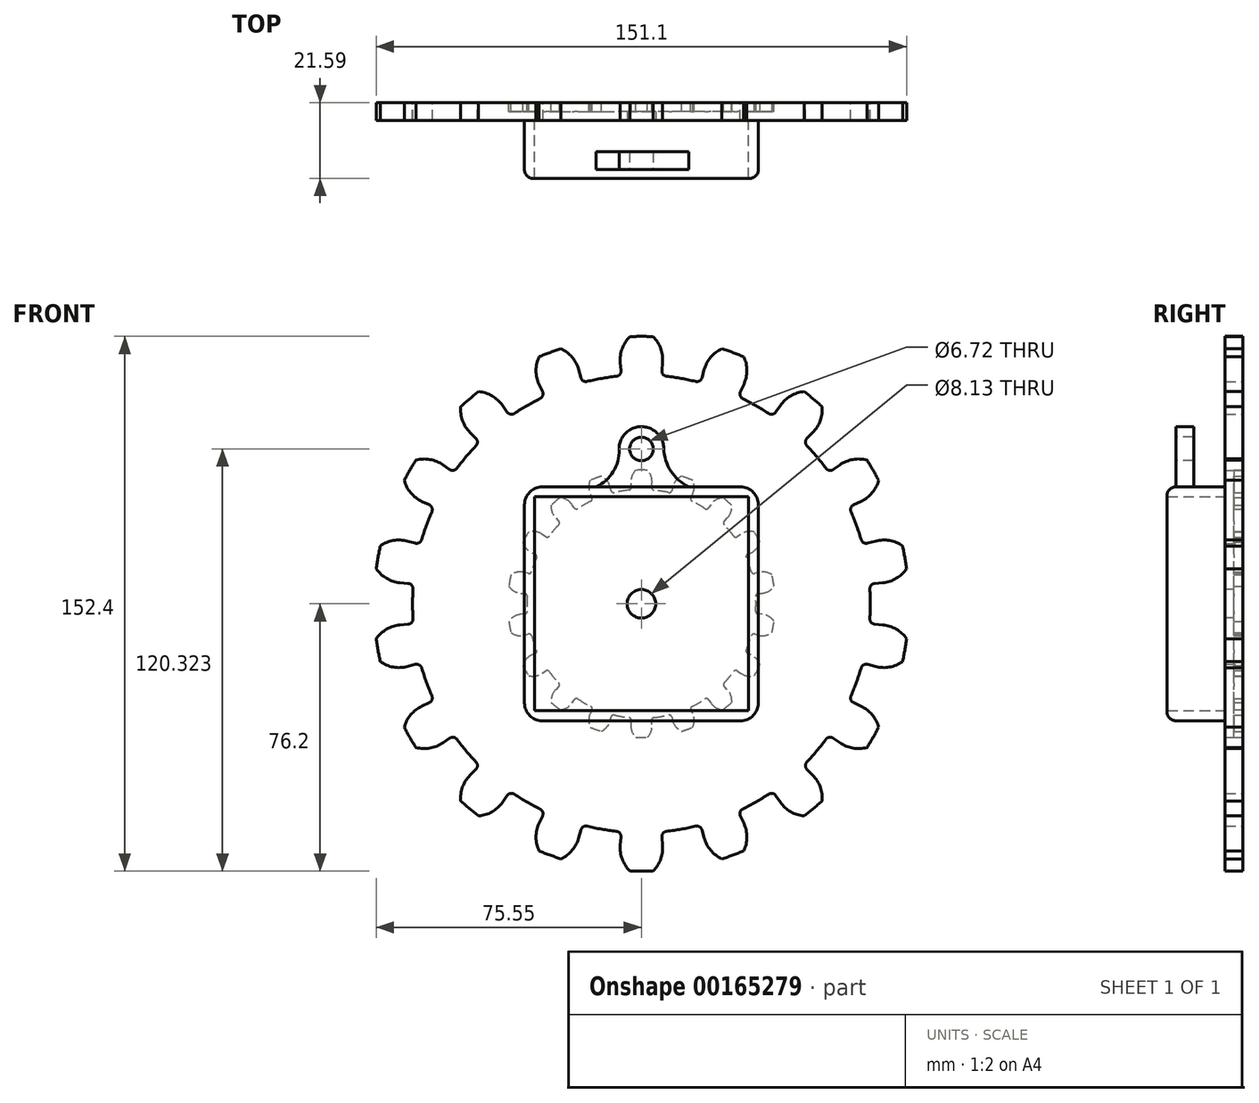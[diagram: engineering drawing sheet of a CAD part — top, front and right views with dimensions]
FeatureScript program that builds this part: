
annotation { "Feature Type Name" : "Feature", "Feature Type Description" : "" }
export const myFeature = defineFeature(function(context is Context, id is Id, definition is map)
    precondition{}
    {
        {
            var Q0;
            Q0=qCreatedBy(makeId("Front.planeOp"),FACE);
            var sketch = newSketch(context, id + "F0", { "sketchPlane" : qUnion([Q0])});
            skArc(sketch, "E0", {"start": v(0, 76.2) * mm, "mid": v(-1.66, 76.18) * mm, "end": v(-3.32, 76.13) * mm});
            skLineSegment(sketch, "E1", {"start": v(0, 0) * mm, "end": v(0, 76.2) * mm, "construction": true});
            skLineSegment(sketch, "E2", {"start": v(0, 0) * mm, "end": v(-11.32, 64.22) * mm});
            skLineSegment(sketch, "E3", {"start": v(0, 0) * mm, "end": v(-6.64, 75.91) * mm, "construction": true});
            skLineSegment(sketch, "E4", {"start": v(0, 0) * mm, "end": v(-3.32, 76.13) * mm, "construction": true});
            skArc(sketch, "E5", {"start": v(-3.32, 76.13) * mm, "mid": v(-5.49, 72.75) * mm, "end": v(-6.02, 68.77) * mm});
            skLineSegment(sketch, "E6", {"start": v(-6.02, 68.77) * mm, "end": v(-5.68, 64.97) * mm, "construction": true});
            skLineSegment(sketch, "E7", {"start": v(-6.02, 68.77) * mm, "end": v(-5.68, 64.97) * mm});
            skLineSegment(sketch, "E8", {"start": v(0, 76.2) * mm, "end": v(0, 0) * mm});
            skArc(sketch, "E9.trimOffspring", {"start": v(-5.68, 64.97) * mm, "mid": v(-8.51, 64.66) * mm, "end": v(-11.32, 64.22) * mm});
            skLineSegment(sketch, "E10.MirrorCS", {"start": v(0, 0) * mm, "end": v(11.32, 64.22) * mm});
            skArc(sketch, "E11.MirrorCS", {"start": v(5.68, 64.97) * mm, "mid": v(8.51, 64.66) * mm, "end": v(11.32, 64.22) * mm});
            skLineSegment(sketch, "E12.MirrorCS", {"start": v(6.02, 68.77) * mm, "end": v(5.68, 64.97) * mm, "construction": true});
            skArc(sketch, "E13.MirrorCS", {"start": v(3.32, 76.13) * mm, "mid": v(5.49, 72.75) * mm, "end": v(6.02, 68.77) * mm});
            skArc(sketch, "E14.MirrorCS", {"start": v(0, 76.2) * mm, "mid": v(1.66, 76.18) * mm, "end": v(3.32, 76.13) * mm});
            skLineSegment(sketch, "E15", {"start": v(5.68, 64.97) * mm, "end": v(6.02, 68.77) * mm});
            skSolve(sketch);
        }
        {
            var Q0;
            Q0 = qSketchRegion(id + "F0", true);
            extrude(context, id + "F1", {"entities" : qUnion([Q0]), "depth" : 12.7 * mm});
        }
        {
            var Q0;
            Q0=makeQuery(id+"F1.opExtrude","SWEPT_EDGE",EDGE,{"disambiguationData":[OSD([sQuery(id+"F0.wireOp",EDGE,"E11.MirrorCS"),sQuery(id+"F0.wireOp",EDGE,"E15")])]});
            var Q1;
            Q1=makeQuery(id+"F1.opExtrude","SWEPT_EDGE",EDGE,{"disambiguationData":[OSD([sQuery(id+"F0.wireOp",EDGE,"E7"),sQuery(id+"F0.wireOp",EDGE,"E9.trimOffspring")])]});
            fillet(context, id + "F2", {"entities" : qUnion([Q0, Q1]), "radius" : 1.52 * mm, "tangentPropagation" : true, "allowEdgeOverflow" : false});
        }
        {
            var Q0;
            Q0=makeQuery(id+"F1.opExtrude","SWEPT_BODY",BODY,{"disambiguationData":[OSD([sQuery(id+"F0.wireOp",EDGE,"E0"),sQuery(id+"F0.wireOp",EDGE,"E2"),sQuery(id+"F0.wireOp",EDGE,"E5"),sQuery(id+"F0.wireOp",EDGE,"E7"),sQuery(id+"F0.wireOp",EDGE,"E9.trimOffspring"),sQuery(id+"F0.wireOp",EDGE,"E10.MirrorCS"),sQuery(id+"F0.wireOp",EDGE,"E11.MirrorCS"),sQuery(id+"F0.wireOp",EDGE,"E13.MirrorCS"),sQuery(id+"F0.wireOp",EDGE,"E14.MirrorCS"),sQuery(id+"F0.wireOp",EDGE,"E15")])]});
            var Q1;
            Q1=makeQuery(id+"F1.opExtrude","SWEPT_EDGE",EDGE,{"disambiguationData":[OSD([sQuery(id+"F0.wireOp",EDGE,"E2"),sQuery(id+"F0.wireOp",EDGE,"E8"),sQuery(id+"F0.wireOp",EDGE,"E10.MirrorCS")])]});
            circularPattern(context, id + "F3", {"operationType" : NewBodyOperationType.ADD, "entities" : qUnion([Q0]), "axis" : qUnion([Q1]), "angle" : 20 * degree, "instanceCount" : 18});
        }
        {
            var Q0;
            {var subQ0=makeQuery(id+"F1.opExtrude","CAP_FACE",FACE,{"disambiguationData":[OSD([sQuery(id+"F0.wireOp",EDGE,"E0"),sQuery(id+"F0.wireOp",EDGE,"E2"),sQuery(id+"F0.wireOp",EDGE,"E5"),sQuery(id+"F0.wireOp",EDGE,"E7"),sQuery(id+"F0.wireOp",EDGE,"E9.trimOffspring"),sQuery(id+"F0.wireOp",EDGE,"E10.MirrorCS"),sQuery(id+"F0.wireOp",EDGE,"E11.MirrorCS"),sQuery(id+"F0.wireOp",EDGE,"E13.MirrorCS"),sQuery(id+"F0.wireOp",EDGE,"E14.MirrorCS"),sQuery(id+"F0.wireOp",EDGE,"E15")])],"isStart":false});Q0=makeQuery(id+"F3.boolean.opBoolean","MERGE",FACE,{"derivedFrom":[subQ0,makeQuery(id+"F3.opPattern","COPY",FACE,{"derivedFrom":subQ0,"instanceName":"1"}),makeQuery(id+"F3.opPattern","COPY",FACE,{"derivedFrom":subQ0,"instanceName":"2"}),makeQuery(id+"F3.opPattern","COPY",FACE,{"derivedFrom":subQ0,"instanceName":"3"}),makeQuery(id+"F3.opPattern","COPY",FACE,{"derivedFrom":subQ0,"instanceName":"4"}),makeQuery(id+"F3.opPattern","COPY",FACE,{"derivedFrom":subQ0,"instanceName":"5"}),makeQuery(id+"F3.opPattern","COPY",FACE,{"derivedFrom":subQ0,"instanceName":"6"}),makeQuery(id+"F3.opPattern","COPY",FACE,{"derivedFrom":subQ0,"instanceName":"7"}),makeQuery(id+"F3.opPattern","COPY",FACE,{"derivedFrom":subQ0,"instanceName":"8"}),makeQuery(id+"F3.opPattern","COPY",FACE,{"derivedFrom":subQ0,"instanceName":"9"}),makeQuery(id+"F3.opPattern","COPY",FACE,{"derivedFrom":subQ0,"instanceName":"10"}),makeQuery(id+"F3.opPattern","COPY",FACE,{"derivedFrom":subQ0,"instanceName":"11"}),makeQuery(id+"F3.opPattern","COPY",FACE,{"derivedFrom":subQ0,"instanceName":"12"}),makeQuery(id+"F3.opPattern","COPY",FACE,{"derivedFrom":subQ0,"instanceName":"13"}),makeQuery(id+"F3.opPattern","COPY",FACE,{"derivedFrom":subQ0,"instanceName":"14"}),makeQuery(id+"F3.opPattern","COPY",FACE,{"derivedFrom":subQ0,"instanceName":"15"}),makeQuery(id+"F3.opPattern","COPY",FACE,{"derivedFrom":subQ0,"instanceName":"16"}),makeQuery(id+"F3.opPattern","COPY",FACE,{"derivedFrom":subQ0,"instanceName":"17"})]});}
            var sketch = newSketch(context, id + "F4", { "sketchPlane" : qUnion([Q0])});
            skLineSegment(sketch, "E16.bottom", {"start": v(-30.48, 30.48) * mm, "end": v(30.48, 30.48) * mm});
            skLineSegment(sketch, "E16.top", {"start": v(-30.48, -30.48) * mm, "end": v(30.48, -30.48) * mm});
            skLineSegment(sketch, "E16.left", {"start": v(-30.48, 30.48) * mm, "end": v(-30.48, -30.48) * mm});
            skLineSegment(sketch, "E16.right", {"start": v(30.48, 30.48) * mm, "end": v(30.48, -30.48) * mm});
            skLineSegment(sketch, "E17", {"start": v(-33.32, 33.32) * mm, "end": v(-33.32, -33.32) * mm});
            skLineSegment(sketch, "E18", {"start": v(-33.32, -33.32) * mm, "end": v(33.32, -33.32) * mm});
            skLineSegment(sketch, "E19", {"start": v(33.32, -33.32) * mm, "end": v(33.32, 33.32) * mm});
            skLineSegment(sketch, "E20", {"start": v(33.32, 33.32) * mm, "end": v(-33.32, 33.32) * mm});
            skLineSegment(sketch, "E21", {"start": v(-30.48, 30.48) * mm, "end": v(30.48, -30.48) * mm, "construction": true});
            skLineSegment(sketch, "E22", {"start": v(-30.48, -30.48) * mm, "end": v(30.48, 30.48) * mm, "construction": true});
            skSolve(sketch);
        }
        {
            var Q0;
            Q0 = qSketchRegion(id + "F4", true);
            extrude(context, id + "F5", {"entities" : qUnion([Q0]), "depth" : 16.5 * mm});
        }
        {
            var Q0;
            {var subQ0=sQuery(id+"F0.wireOp",EDGE,"E15");var subQ1=sQuery(id+"F0.wireOp",EDGE,"E11.MirrorCS");var subQ3=sQuery(id+"F0.wireOp",EDGE,"E13.MirrorCS");var subQ5=sQuery(id+"F0.wireOp",EDGE,"E14.MirrorCS");var subQ6=sQuery(id+"F0.wireOp",EDGE,"E0");var subQ12=sQuery(id+"F0.wireOp",EDGE,"E7");var subQ15=sQuery(id+"F0.wireOp",EDGE,"E9.trimOffspring");var subQ19=sQuery(id+"F0.wireOp",EDGE,"E5");var subQ20=makeQuery(id+"F1.opExtrude","SWEPT_FACE",FACE,{"disambiguationData":[OSD([subQ19])]});var subQ21=makeQuery(id+"F1.opExtrude","CAP_FACE",FACE,{"disambiguationData":[OSD([subQ6,sQuery(id+"F0.wireOp",EDGE,"E2"),subQ19,subQ12,subQ15,sQuery(id+"F0.wireOp",EDGE,"E10.MirrorCS"),subQ1,subQ3,subQ5,subQ0])],"isStart":false});Q0=makeQuery(id+"F5.boolean.opBoolean","SPLIT",FACE,{"disambiguationData":[TD([subQ20])],"derivedFrom":makeQuery(id+"F3.boolean.opBoolean","MERGE",FACE,{"derivedFrom":[subQ21,makeQuery(id+"F3.opPattern","COPY",FACE,{"derivedFrom":subQ21,"instanceName":"1"}),makeQuery(id+"F3.opPattern","COPY",FACE,{"derivedFrom":subQ21,"instanceName":"2"}),makeQuery(id+"F3.opPattern","COPY",FACE,{"derivedFrom":subQ21,"instanceName":"3"}),makeQuery(id+"F3.opPattern","COPY",FACE,{"derivedFrom":subQ21,"instanceName":"4"}),makeQuery(id+"F3.opPattern","COPY",FACE,{"derivedFrom":subQ21,"instanceName":"5"}),makeQuery(id+"F3.opPattern","COPY",FACE,{"derivedFrom":subQ21,"instanceName":"6"}),makeQuery(id+"F3.opPattern","COPY",FACE,{"derivedFrom":subQ21,"instanceName":"7"}),makeQuery(id+"F3.opPattern","COPY",FACE,{"derivedFrom":subQ21,"instanceName":"8"}),makeQuery(id+"F3.opPattern","COPY",FACE,{"derivedFrom":subQ21,"instanceName":"9"}),makeQuery(id+"F3.opPattern","COPY",FACE,{"derivedFrom":subQ21,"instanceName":"10"}),makeQuery(id+"F3.opPattern","COPY",FACE,{"derivedFrom":subQ21,"instanceName":"11"}),makeQuery(id+"F3.opPattern","COPY",FACE,{"derivedFrom":subQ21,"instanceName":"12"}),makeQuery(id+"F3.opPattern","COPY",FACE,{"derivedFrom":subQ21,"instanceName":"13"}),makeQuery(id+"F3.opPattern","COPY",FACE,{"derivedFrom":subQ21,"instanceName":"14"}),makeQuery(id+"F3.opPattern","COPY",FACE,{"derivedFrom":subQ21,"instanceName":"15"}),makeQuery(id+"F3.opPattern","COPY",FACE,{"derivedFrom":subQ21,"instanceName":"16"}),makeQuery(id+"F3.opPattern","COPY",FACE,{"derivedFrom":subQ21,"instanceName":"17"})]})});}
            var sketch = newSketch(context, id + "F6", { "sketchPlane" : qUnion([Q0])});
            skCircle(sketch, "E23", {"center": v(0, 0) * mm, "radius": 4.06 * mm});
            skSolve(sketch);
        }
        {
            var Q0;
            Q0 = qSketchRegion(id + "F6", true);
            extrude(context, id + "F7", {"entities" : qUnion([Q0]), "operationType" : NewBodyOperationType.REMOVE, "oppositeDirection" : true, "depth" : 25.4 * mm});
        }
        {
            var Q0;
            Q0=makeQuery(id+"F5.opExtrude","SWEPT_EDGE",EDGE,{"disambiguationData":[OSD([sQuery(id+"F4.wireOp",EDGE,"E19"),sQuery(id+"F4.wireOp",EDGE,"E20")])]});
            var Q1;
            Q1=makeQuery(id+"F5.opExtrude","SWEPT_EDGE",EDGE,{"disambiguationData":[OSD([sQuery(id+"F4.wireOp",EDGE,"E17"),sQuery(id+"F4.wireOp",EDGE,"E20")])]});
            var Q2;
            Q2=makeQuery(id+"F5.opExtrude","SWEPT_EDGE",EDGE,{"disambiguationData":[OSD([sQuery(id+"F4.wireOp",EDGE,"E17"),sQuery(id+"F4.wireOp",EDGE,"E18")])]});
            var Q3;
            Q3=makeQuery(id+"F5.opExtrude","SWEPT_EDGE",EDGE,{"disambiguationData":[OSD([sQuery(id+"F4.wireOp",EDGE,"E18"),sQuery(id+"F4.wireOp",EDGE,"E19")])]});
            fillet(context, id + "F8", {"entities" : qUnion([Q0, Q1, Q2, Q3]), "radius" : 5.08 * mm, "tangentPropagation" : true, "allowEdgeOverflow" : false});
        }
        {
            var Q0;
            Q0=makeQuery(id+"F5.opExtrude","CAP_EDGE",EDGE,{"disambiguationData":[OSD([sQuery(id+"F4.wireOp",EDGE,"E18")])],"isStart":false});
            var Q1;
            Q1=makeQuery(id+"F5.opExtrude","CAP_EDGE",EDGE,{"disambiguationData":[OSD([sQuery(id+"F4.wireOp",EDGE,"E19")])],"isStart":false});
            var Q2;
            Q2=makeQuery(id+"F5.opExtrude","CAP_EDGE",EDGE,{"disambiguationData":[OSD([sQuery(id+"F4.wireOp",EDGE,"E20")])],"isStart":false});
            var Q3;
            Q3=makeQuery(id+"F5.opExtrude","CAP_EDGE",EDGE,{"disambiguationData":[OSD([sQuery(id+"F4.wireOp",EDGE,"E17")])],"isStart":false});
            var Q4;
            {var subQ0=sQuery(id+"F4.wireOp",EDGE,"E18");var subQ1=sQuery(id+"F4.wireOp",EDGE,"E17");Q4=makeQuery(id+"F8.opFillet","BLEND_EDGE",EDGE,{"blendedFrom":[makeQuery(id+"F5.opExtrude","SWEPT_EDGE",EDGE,{"disambiguationData":[OSD([subQ1,subQ0])]}),makeQuery(id+"F5.opExtrude","CAP_FACE",FACE,{"disambiguationData":[OSD([sQuery(id+"F4.wireOp",EDGE,"E16.bottom"),sQuery(id+"F4.wireOp",EDGE,"E16.top"),sQuery(id+"F4.wireOp",EDGE,"E16.left"),sQuery(id+"F4.wireOp",EDGE,"E16.right"),subQ1,subQ0,sQuery(id+"F4.wireOp",EDGE,"E19"),sQuery(id+"F4.wireOp",EDGE,"E20")])],"isStart":false})],"blendedInto":[makeQuery(id+"F5.opExtrude","CAP_FACE",FACE,{"disambiguationData":[OSD([sQuery(id+"F4.wireOp",EDGE,"E16.bottom"),sQuery(id+"F4.wireOp",EDGE,"E16.top"),sQuery(id+"F4.wireOp",EDGE,"E16.left"),sQuery(id+"F4.wireOp",EDGE,"E16.right"),subQ1,subQ0,sQuery(id+"F4.wireOp",EDGE,"E19"),sQuery(id+"F4.wireOp",EDGE,"E20")])],"isStart":false})]});}
            var Q5;
            {var subQ0=sQuery(id+"F4.wireOp",EDGE,"E19");var subQ1=sQuery(id+"F4.wireOp",EDGE,"E18");Q5=makeQuery(id+"F8.opFillet","BLEND_EDGE",EDGE,{"blendedFrom":[makeQuery(id+"F5.opExtrude","SWEPT_EDGE",EDGE,{"disambiguationData":[OSD([subQ1,subQ0])]}),makeQuery(id+"F5.opExtrude","CAP_FACE",FACE,{"disambiguationData":[OSD([sQuery(id+"F4.wireOp",EDGE,"E16.bottom"),sQuery(id+"F4.wireOp",EDGE,"E16.top"),sQuery(id+"F4.wireOp",EDGE,"E16.left"),sQuery(id+"F4.wireOp",EDGE,"E16.right"),sQuery(id+"F4.wireOp",EDGE,"E17"),subQ1,subQ0,sQuery(id+"F4.wireOp",EDGE,"E20")])],"isStart":false})],"blendedInto":[makeQuery(id+"F5.opExtrude","CAP_FACE",FACE,{"disambiguationData":[OSD([sQuery(id+"F4.wireOp",EDGE,"E16.bottom"),sQuery(id+"F4.wireOp",EDGE,"E16.top"),sQuery(id+"F4.wireOp",EDGE,"E16.left"),sQuery(id+"F4.wireOp",EDGE,"E16.right"),sQuery(id+"F4.wireOp",EDGE,"E17"),subQ1,subQ0,sQuery(id+"F4.wireOp",EDGE,"E20")])],"isStart":false})]});}
            var Q6;
            {var subQ0=sQuery(id+"F4.wireOp",EDGE,"E20");var subQ1=sQuery(id+"F4.wireOp",EDGE,"E19");Q6=makeQuery(id+"F8.opFillet","BLEND_EDGE",EDGE,{"blendedFrom":[makeQuery(id+"F5.opExtrude","SWEPT_EDGE",EDGE,{"disambiguationData":[OSD([subQ1,subQ0])]}),makeQuery(id+"F5.opExtrude","CAP_FACE",FACE,{"disambiguationData":[OSD([sQuery(id+"F4.wireOp",EDGE,"E16.bottom"),sQuery(id+"F4.wireOp",EDGE,"E16.top"),sQuery(id+"F4.wireOp",EDGE,"E16.left"),sQuery(id+"F4.wireOp",EDGE,"E16.right"),sQuery(id+"F4.wireOp",EDGE,"E17"),sQuery(id+"F4.wireOp",EDGE,"E18"),subQ1,subQ0])],"isStart":false})],"blendedInto":[makeQuery(id+"F5.opExtrude","CAP_FACE",FACE,{"disambiguationData":[OSD([sQuery(id+"F4.wireOp",EDGE,"E16.bottom"),sQuery(id+"F4.wireOp",EDGE,"E16.top"),sQuery(id+"F4.wireOp",EDGE,"E16.left"),sQuery(id+"F4.wireOp",EDGE,"E16.right"),sQuery(id+"F4.wireOp",EDGE,"E17"),sQuery(id+"F4.wireOp",EDGE,"E18"),subQ1,subQ0])],"isStart":false})]});}
            var Q7;
            {var subQ0=sQuery(id+"F4.wireOp",EDGE,"E20");var subQ1=sQuery(id+"F4.wireOp",EDGE,"E17");Q7=makeQuery(id+"F8.opFillet","BLEND_EDGE",EDGE,{"blendedFrom":[makeQuery(id+"F5.opExtrude","SWEPT_EDGE",EDGE,{"disambiguationData":[OSD([subQ1,subQ0])]}),makeQuery(id+"F5.opExtrude","CAP_FACE",FACE,{"disambiguationData":[OSD([sQuery(id+"F4.wireOp",EDGE,"E16.bottom"),sQuery(id+"F4.wireOp",EDGE,"E16.top"),sQuery(id+"F4.wireOp",EDGE,"E16.left"),sQuery(id+"F4.wireOp",EDGE,"E16.right"),subQ1,sQuery(id+"F4.wireOp",EDGE,"E18"),sQuery(id+"F4.wireOp",EDGE,"E19"),subQ0])],"isStart":false})],"blendedInto":[makeQuery(id+"F5.opExtrude","CAP_FACE",FACE,{"disambiguationData":[OSD([sQuery(id+"F4.wireOp",EDGE,"E16.bottom"),sQuery(id+"F4.wireOp",EDGE,"E16.top"),sQuery(id+"F4.wireOp",EDGE,"E16.left"),sQuery(id+"F4.wireOp",EDGE,"E16.right"),subQ1,sQuery(id+"F4.wireOp",EDGE,"E18"),sQuery(id+"F4.wireOp",EDGE,"E19"),subQ0])],"isStart":false})]});}
            fillet(context, id + "F9", {"entities" : qUnion([Q0, Q1, Q2, Q3, Q4, Q5, Q6, Q7]), "radius" : 2.54 * mm, "tangentPropagation" : true, "allowEdgeOverflow" : false});
        }
        {
            var Q0;
            Q0=makeQuery(id+"F5.opExtrude","CAP_FACE",FACE,{"disambiguationData":[OSD([sQuery(id+"F4.wireOp",EDGE,"E16.bottom"),sQuery(id+"F4.wireOp",EDGE,"E16.top"),sQuery(id+"F4.wireOp",EDGE,"E16.left"),sQuery(id+"F4.wireOp",EDGE,"E16.right"),sQuery(id+"F4.wireOp",EDGE,"E17"),sQuery(id+"F4.wireOp",EDGE,"E18"),sQuery(id+"F4.wireOp",EDGE,"E19"),sQuery(id+"F4.wireOp",EDGE,"E20")])],"isStart":false});
            var sketch = newSketch(context, id + "F10", { "sketchPlane" : qUnion([Q0])});
            skArc(sketch, "E24", {"start": v(6.36, 44.3) * mm, "mid": v(-0.18, 50.48) * mm, "end": v(-6.36, 43.93) * mm});
            skCircle(sketch, "E25", {"center": v(0, 44.12) * mm, "radius": 3.36 * mm});
            skArc(sketch, "E26", {"start": v(-12.9, 33.32) * mm, "mid": v(-8.04, 37.65) * mm, "end": v(-6.36, 43.93) * mm});
            skArc(sketch, "E27", {"start": v(6.36, 44.3) * mm, "mid": v(8.39, 37.8) * mm, "end": v(13.51, 33.32) * mm});
            skLineSegment(sketch, "E28", {"start": v(-6.04, 33.32) * mm, "end": v(-12.9, 33.32) * mm});
            skLineSegment(sketch, "E29", {"start": v(6.66, 33.32) * mm, "end": v(13.51, 33.32) * mm});
            skLineSegment(sketch, "E30", {"start": v(-12.9, 33.32) * mm, "end": v(13.51, 33.32) * mm});
            skSolve(sketch);
        }
        {
            var Q0;
            Q0 = qSketchRegion(id + "F10", true);
            extrude(context, id + "F11", {"entities" : qUnion([Q0]), "oppositeDirection" : true, "depth" : 5.08 * mm});
        }
        {
            var Q0;
            Q0=makeQuery(id+"F1.opExtrude","SWEPT_BODY",BODY,{"disambiguationData":[OSD([sQuery(id+"F0.wireOp",EDGE,"E0"),sQuery(id+"F0.wireOp",EDGE,"E2"),sQuery(id+"F0.wireOp",EDGE,"E5"),sQuery(id+"F0.wireOp",EDGE,"E7"),sQuery(id+"F0.wireOp",EDGE,"E9.trimOffspring"),sQuery(id+"F0.wireOp",EDGE,"E10.MirrorCS"),sQuery(id+"F0.wireOp",EDGE,"E11.MirrorCS"),sQuery(id+"F0.wireOp",EDGE,"E13.MirrorCS"),sQuery(id+"F0.wireOp",EDGE,"E14.MirrorCS"),sQuery(id+"F0.wireOp",EDGE,"E15")])]});
            var Q1;
            Q1=qCreatedBy(makeId("Origin.pointOp"),VERTEX);
            transform(context, id + "F12", {"entities" : qUnion([Q0]), "transformType" : TransformType.SCALE_UNIFORMLY, "scale" : .5, "scalePoint" : qUnion([Q1]), "makeCopy" : true});
        }
        {
            var Q0;
            {var subQ0=makeQuery(id+"F1.opExtrude","CAP_FACE",FACE,{"disambiguationData":[OSD([sQuery(id+"F0.wireOp",EDGE,"E0"),sQuery(id+"F0.wireOp",EDGE,"E2"),sQuery(id+"F0.wireOp",EDGE,"E5"),sQuery(id+"F0.wireOp",EDGE,"E7"),sQuery(id+"F0.wireOp",EDGE,"E9.trimOffspring"),sQuery(id+"F0.wireOp",EDGE,"E10.MirrorCS"),sQuery(id+"F0.wireOp",EDGE,"E11.MirrorCS"),sQuery(id+"F0.wireOp",EDGE,"E13.MirrorCS"),sQuery(id+"F0.wireOp",EDGE,"E14.MirrorCS"),sQuery(id+"F0.wireOp",EDGE,"E15")])],"isStart":true});Q0=makeQuery(id+"F12.opPattern","COPY",FACE,{"derivedFrom":makeQuery(id+"F3.boolean.opBoolean","MERGE",FACE,{"derivedFrom":[subQ0,makeQuery(id+"F3.opPattern","COPY",FACE,{"derivedFrom":subQ0,"instanceName":"1"}),makeQuery(id+"F3.opPattern","COPY",FACE,{"derivedFrom":subQ0,"instanceName":"2"}),makeQuery(id+"F3.opPattern","COPY",FACE,{"derivedFrom":subQ0,"instanceName":"3"}),makeQuery(id+"F3.opPattern","COPY",FACE,{"derivedFrom":subQ0,"instanceName":"4"}),makeQuery(id+"F3.opPattern","COPY",FACE,{"derivedFrom":subQ0,"instanceName":"5"}),makeQuery(id+"F3.opPattern","COPY",FACE,{"derivedFrom":subQ0,"instanceName":"6"}),makeQuery(id+"F3.opPattern","COPY",FACE,{"derivedFrom":subQ0,"instanceName":"7"}),makeQuery(id+"F3.opPattern","COPY",FACE,{"derivedFrom":subQ0,"instanceName":"8"}),makeQuery(id+"F3.opPattern","COPY",FACE,{"derivedFrom":subQ0,"instanceName":"9"}),makeQuery(id+"F3.opPattern","COPY",FACE,{"derivedFrom":subQ0,"instanceName":"10"}),makeQuery(id+"F3.opPattern","COPY",FACE,{"derivedFrom":subQ0,"instanceName":"11"}),makeQuery(id+"F3.opPattern","COPY",FACE,{"derivedFrom":subQ0,"instanceName":"12"}),makeQuery(id+"F3.opPattern","COPY",FACE,{"derivedFrom":subQ0,"instanceName":"13"}),makeQuery(id+"F3.opPattern","COPY",FACE,{"derivedFrom":subQ0,"instanceName":"14"}),makeQuery(id+"F3.opPattern","COPY",FACE,{"derivedFrom":subQ0,"instanceName":"15"}),makeQuery(id+"F3.opPattern","COPY",FACE,{"derivedFrom":subQ0,"instanceName":"16"}),makeQuery(id+"F3.opPattern","COPY",FACE,{"derivedFrom":subQ0,"instanceName":"17"})]}),"instanceName":"1"});}
            extrude(context, id + "F13", {"entities" : qUnion([Q0]), "operationType" : NewBodyOperationType.REMOVE, "oppositeDirection" : true, "depth" : 2.54 * mm});
        }
        {
            var Q0;
            Q0=makeQuery(id+"F1.opExtrude","SWEPT_BODY",BODY,{"disambiguationData":[OSD([sQuery(id+"F0.wireOp",EDGE,"E0"),sQuery(id+"F0.wireOp",EDGE,"E2"),sQuery(id+"F0.wireOp",EDGE,"E5"),sQuery(id+"F0.wireOp",EDGE,"E7"),sQuery(id+"F0.wireOp",EDGE,"E9.trimOffspring"),sQuery(id+"F0.wireOp",EDGE,"E10.MirrorCS"),sQuery(id+"F0.wireOp",EDGE,"E11.MirrorCS"),sQuery(id+"F0.wireOp",EDGE,"E13.MirrorCS"),sQuery(id+"F0.wireOp",EDGE,"E14.MirrorCS"),sQuery(id+"F0.wireOp",EDGE,"E15")])]});
            var Q1;
            Q1=makeQuery(id+"F12.opPattern","COPY",BODY,{"derivedFrom":makeQuery(id+"F1.opExtrude","SWEPT_BODY",BODY,{"disambiguationData":[OSD([sQuery(id+"F0.wireOp",EDGE,"E0"),sQuery(id+"F0.wireOp",EDGE,"E2"),sQuery(id+"F0.wireOp",EDGE,"E5"),sQuery(id+"F0.wireOp",EDGE,"E7"),sQuery(id+"F0.wireOp",EDGE,"E9.trimOffspring"),sQuery(id+"F0.wireOp",EDGE,"E10.MirrorCS"),sQuery(id+"F0.wireOp",EDGE,"E11.MirrorCS"),sQuery(id+"F0.wireOp",EDGE,"E13.MirrorCS"),sQuery(id+"F0.wireOp",EDGE,"E14.MirrorCS"),sQuery(id+"F0.wireOp",EDGE,"E15")])]}),"instanceName":"1"});
            booleanBodies(context, id + "F14", {"operationType" : BooleanOperationType.UNION, "tools" : qUnion([Q0, Q1])});
        }
        {
            var Q0;
            Q0 = qSketchRegion(id + "F6", true);
            extrude(context, id + "F15", {"entities" : qUnion([Q0]), "operationType" : NewBodyOperationType.REMOVE, "oppositeDirection" : true, "depth" : 25.4 * mm});
        }
        {
            var Q0;
            Q0=makeQuery(id+"F11.opExtrude","SWEPT_BODY",BODY,{"disambiguationData":[OSD([sQuery(id+"F10.wireOp",EDGE,"E24"),sQuery(id+"F10.wireOp",EDGE,"E25"),sQuery(id+"F10.wireOp",EDGE,"E26"),sQuery(id+"F10.wireOp",EDGE,"E27"),sQuery(id+"F10.wireOp",EDGE,"E30")])]});
            transform(context, id + "F16", {"entities" : qUnion([Q0]), "transformType" : TransformType.TRANSLATION_3D, "dx" : 0 * mm, "dy" : 2.54 * mm, "dz" : 0 * mm, "makeCopy" : false});
        }
        {
            var Q0;
            {var subQ0=sQuery(id+"F0.wireOp",EDGE,"E15");var subQ1=sQuery(id+"F0.wireOp",EDGE,"E11.MirrorCS");var subQ3=sQuery(id+"F0.wireOp",EDGE,"E13.MirrorCS");var subQ5=sQuery(id+"F0.wireOp",EDGE,"E14.MirrorCS");var subQ6=sQuery(id+"F0.wireOp",EDGE,"E0");var subQ8=sQuery(id+"F0.wireOp",EDGE,"E7");var subQ10=sQuery(id+"F0.wireOp",EDGE,"E9.trimOffspring");var subQ13=sQuery(id+"F0.wireOp",EDGE,"E5");var subQ14=makeQuery(id+"F1.opExtrude","SWEPT_FACE",FACE,{"disambiguationData":[OSD([subQ13])]});var subQ17=makeQuery(id+"F7.boolean.opBoolean","COPY",FACE,{"derivedFrom":makeQuery(id+"F7.opExtrude","SWEPT_FACE",FACE,{"disambiguationData":[OSD([sQuery(id+"F6.wireOp",EDGE,"E23")])]})});var subQ18=sQuery(id+"F0.wireOp",EDGE,"E10.MirrorCS");var subQ19=sQuery(id+"F0.wireOp",EDGE,"E2");var subQ20=makeQuery(id+"F13.opExtrude","CAP_FACE",FACE,{"disambiguationData":[OSD([subQ6,subQ19,subQ13,subQ8,subQ10,subQ18,subQ1,subQ3,subQ5,subQ0])],"isStart":false});Q0=makeQuery(id+"F14.opBoolean","MERGE",FACE,{"derivedFrom":[makeQuery(id+"F13.boolean.opBoolean","COPY",FACE,{"disambiguationData":[TD([subQ17])],"derivedFrom":subQ20}),makeQuery(id+"F13.boolean.opBoolean","COPY",FACE,{"disambiguationData":[TD([makeQuery(id+"F12.opPattern","COPY",FACE,{"derivedFrom":subQ14,"instanceName":"1"})])],"derivedFrom":subQ20})]});}
            extrude(context, id + "F17", {"entities" : qUnion([Q0]), "operationType" : NewBodyOperationType.REMOVE, "oppositeDirection" : true, "depth" : 7.62 * mm});
        }
        {
            var Q0;
            {var subQ0=makeQuery(id+"F1.opExtrude","CAP_FACE",FACE,{"disambiguationData":[OSD([sQuery(id+"F0.wireOp",EDGE,"E0"),sQuery(id+"F0.wireOp",EDGE,"E2"),sQuery(id+"F0.wireOp",EDGE,"E5"),sQuery(id+"F0.wireOp",EDGE,"E7"),sQuery(id+"F0.wireOp",EDGE,"E9.trimOffspring"),sQuery(id+"F0.wireOp",EDGE,"E10.MirrorCS"),sQuery(id+"F0.wireOp",EDGE,"E11.MirrorCS"),sQuery(id+"F0.wireOp",EDGE,"E13.MirrorCS"),sQuery(id+"F0.wireOp",EDGE,"E14.MirrorCS"),sQuery(id+"F0.wireOp",EDGE,"E15")])],"isStart":true});Q0=makeQuery(id+"F3.boolean.opBoolean","MERGE",FACE,{"derivedFrom":[subQ0,makeQuery(id+"F3.opPattern","COPY",FACE,{"derivedFrom":subQ0,"instanceName":"1"}),makeQuery(id+"F3.opPattern","COPY",FACE,{"derivedFrom":subQ0,"instanceName":"2"}),makeQuery(id+"F3.opPattern","COPY",FACE,{"derivedFrom":subQ0,"instanceName":"3"}),makeQuery(id+"F3.opPattern","COPY",FACE,{"derivedFrom":subQ0,"instanceName":"4"}),makeQuery(id+"F3.opPattern","COPY",FACE,{"derivedFrom":subQ0,"instanceName":"5"}),makeQuery(id+"F3.opPattern","COPY",FACE,{"derivedFrom":subQ0,"instanceName":"6"}),makeQuery(id+"F3.opPattern","COPY",FACE,{"derivedFrom":subQ0,"instanceName":"7"}),makeQuery(id+"F3.opPattern","COPY",FACE,{"derivedFrom":subQ0,"instanceName":"8"}),makeQuery(id+"F3.opPattern","COPY",FACE,{"derivedFrom":subQ0,"instanceName":"9"}),makeQuery(id+"F3.opPattern","COPY",FACE,{"derivedFrom":subQ0,"instanceName":"10"}),makeQuery(id+"F3.opPattern","COPY",FACE,{"derivedFrom":subQ0,"instanceName":"11"}),makeQuery(id+"F3.opPattern","COPY",FACE,{"derivedFrom":subQ0,"instanceName":"12"}),makeQuery(id+"F3.opPattern","COPY",FACE,{"derivedFrom":subQ0,"instanceName":"13"}),makeQuery(id+"F3.opPattern","COPY",FACE,{"derivedFrom":subQ0,"instanceName":"14"}),makeQuery(id+"F3.opPattern","COPY",FACE,{"derivedFrom":subQ0,"instanceName":"15"}),makeQuery(id+"F3.opPattern","COPY",FACE,{"derivedFrom":subQ0,"instanceName":"16"}),makeQuery(id+"F3.opPattern","COPY",FACE,{"derivedFrom":subQ0,"instanceName":"17"})]});}
            extrude(context, id + "F18", {"entities" : qUnion([Q0]), "operationType" : NewBodyOperationType.REMOVE, "oppositeDirection" : true, "depth" : 7.62 * mm});
        }
    });
